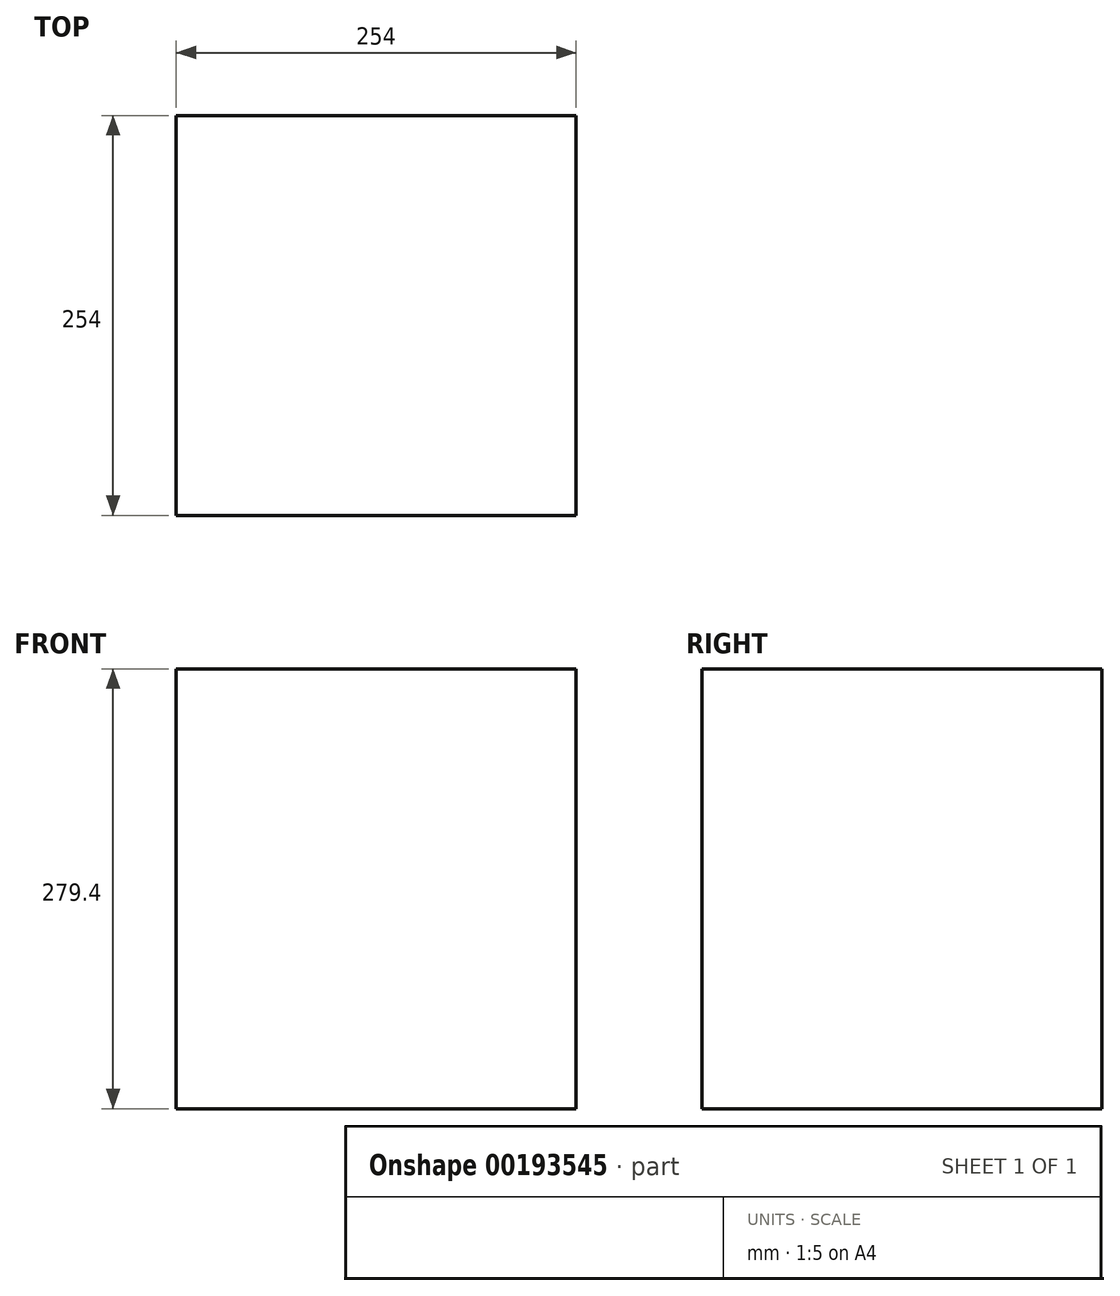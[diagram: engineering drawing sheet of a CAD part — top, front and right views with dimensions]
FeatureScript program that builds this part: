
annotation { "Feature Type Name" : "Feature", "Feature Type Description" : "" }
export const myFeature = defineFeature(function(context is Context, id is Id, definition is map)
    precondition{}
    {
        {
            var Q0;
            Q0=qCreatedBy(makeId("Top.planeOp"),FACE);
            var sketch = newSketch(context, id + "F0", { "sketchPlane" : qUnion([Q0])});
            skPoint(sketch, "E0.middle", {"position": v(0, 0) * mm});
            skPoint(sketch, "E0.left.start.orphan", {"position": v(299.2, 126.59) * mm});
            skPoint(sketch, "E0.top.start.orphan", {"position": v(299.2, -126.59) * mm});
            skPoint(sketch, "E0.right.end.orphan", {"position": v(-299.2, -126.59) * mm});
            skPoint(sketch, "E0.right.start.orphan", {"position": v(-299.2, 126.59) * mm});
            skPoint(sketch, "E1.left.end.orphan", {"position": v(-150.94, 211.02) * mm});
            skPoint(sketch, "E1.bottom.start.orphan", {"position": v(-150.94, 42.16) * mm});
            skPoint(sketch, "E1.right.end.orphan", {"position": v(-447.47, 211.02) * mm});
            skPoint(sketch, "E1.right.start.orphan", {"position": v(-447.47, 42.16) * mm});
            skLineSegment(sketch, "E2.bottom", {"start": v(127, 127) * mm, "end": v(-127, 127) * mm});
            skLineSegment(sketch, "E2.top", {"start": v(127, -127) * mm, "end": v(-127, -127) * mm});
            skLineSegment(sketch, "E2.left", {"start": v(127, 127) * mm, "end": v(127, -127) * mm});
            skLineSegment(sketch, "E2.right", {"start": v(-127, 127) * mm, "end": v(-127, -127) * mm});
            skSolve(sketch);
        }
        {
            var Q0;
            Q0 = qSketchRegion(id + "F0", true);
            extrude(context, id + "F1", {"entities" : qUnion([Q0]), "depth" : 25.4 * mm});
        }
        {
            var Q0;
            Q0=makeQuery(id+"F1.opExtrude","CAP_FACE",FACE,{"disambiguationData":[OSD([sQuery(id+"F0.wireOp",EDGE,"E2.bottom"),sQuery(id+"F0.wireOp",EDGE,"E2.top"),sQuery(id+"F0.wireOp",EDGE,"E2.left"),sQuery(id+"F0.wireOp",EDGE,"E2.right")])],"isStart":false});
            extrude(context, id + "F2", {"entities" : qUnion([Q0]), "operationType" : NewBodyOperationType.ADD, "depth" : 254 * mm});
        }
    });
